FCSTD DOCUMENT  (FreeCAD 0.20R26155 (Git))
Label: AVX-009159010061911 
License: All rights reserved
LicenseURL: http://en.wikipedia.org/wiki/All_rights_reserved
objects: Sketcher::SketchObject×2, PartDesign::Body×1
note: 3 computed .brp shape members not serialized (recipe doc carries the construction recipe); baked Part::Feature solids carry a one-line shape summary decoded from their .brp

FEATURE [Sketcher::SketchObject] Sketch  label="Edge_Cuts_0.1"
  FullyConstrained = false
  MapMode = 5
  Support = -> [XY_Plane]
  sketch-geometry (7):
    g0: LineSegment StartX=0 StartY=5.09886 StartZ=0 EndX=3.7 EndY=5.09886 EndZ=0
    g1: ArcOfCircle CenterX=4 CenterY=2.29886 CenterZ=0 NormalX=0 NormalY=0 NormalZ=1 AngleXU=0 Radius=0.3 StartAngle=3.14159 EndAngle=6.28319
    g2: LineSegment StartX=3.7 StartY=5.09886 StartZ=0 EndX=3.7 EndY=2.29886 EndZ=0
    g3: LineSegment StartX=4.3 StartY=2.29886 StartZ=0 EndX=4.3 EndY=5.09886 EndZ=0
    g4: LineSegment StartX=4 StartY=5.09886 StartZ=0 EndX=4 EndY=2.29886 EndZ=0
    g5: LineSegment StartX=4.3 StartY=5.09886 StartZ=0 EndX=10 EndY=5.09886 EndZ=0
    g6: LineSegment StartX=3.7 StartY=5.09886 StartZ=0 EndX=4.3 EndY=5.09886 EndZ=0
  constraints (19):
    c: PointOnObject(g0,g-2)
    c: Horizontal(g0)
    c: DistanceX(g0,g5) = 10
    c: Tangent(g2,g1) = -1.5708
    c: Tangent(g1,g3) = -1.5708
    c: Coincident(g4,g1)
    c: Vertical(g4)
    c: Diameter(g1) = 0.6
    c: Coincident(g5,g3)
    c: Coincident(g0,g2)
    c: Vertical(g3)
    c: Vertical(g2)
    c: Horizontal(g5)
    c: Coincident(g6,g0)
    c: Coincident(g6,g3)
    c: Horizontal(g6)
    c: PointOnObject(g4,g6)
    c: DistanceY(g4,g4) = 2.8
    c: DistanceX(g0,g4) = 4
FEATURE [Sketcher::SketchObject] Sketch001  label="Pads_TH_SMD"
  ExternalGeometry = -> [Sketch]
  FullyConstrained = false
  MapMode = 5
  Support = -> [XY_Plane]
  sketch-geometry (26):
    g0: LineSegment StartX=0 StartY=4.59886 StartZ=0 EndX=10.0102 EndY=4.59886 EndZ=0
    g1: LineSegment StartX=0.5 StartY=4.59886 StartZ=0 EndX=1.5 EndY=4.59886 EndZ=0
    g2: LineSegment StartX=1.5 StartY=4.59886 StartZ=0 EndX=1.5 EndY=0.598863 EndZ=0
    g3: LineSegment StartX=1.5 StartY=0.598863 StartZ=0 EndX=0.5 EndY=0.598863 EndZ=0
    g4: LineSegment StartX=0.5 StartY=0.598863 StartZ=0 EndX=0.5 EndY=4.59886 EndZ=0
    g5: LineSegment StartX=2.5 StartY=4.59886 StartZ=0 EndX=3.5 EndY=4.59886 EndZ=0
    g6: LineSegment StartX=3.5 StartY=4.59886 StartZ=0 EndX=3.5 EndY=0.598863 EndZ=0
    g7: LineSegment StartX=3.5 StartY=0.598863 StartZ=0 EndX=2.5 EndY=0.598863 EndZ=0
    g8: LineSegment StartX=2.5 StartY=0.598863 StartZ=0 EndX=2.5 EndY=4.59886 EndZ=0
    g9: LineSegment StartX=4.5 StartY=4.59886 StartZ=0 EndX=5.5 EndY=4.59886 EndZ=0
    g10: LineSegment StartX=5.5 StartY=4.59886 StartZ=0 EndX=5.5 EndY=0.598863 EndZ=0
    g11: LineSegment StartX=5.5 StartY=0.598863 StartZ=0 EndX=4.5 EndY=0.598863 EndZ=0
    g12: LineSegment StartX=4.5 StartY=0.598863 StartZ=0 EndX=4.5 EndY=4.59886 EndZ=0
    g13: LineSegment StartX=6.5 StartY=4.59886 StartZ=0 EndX=7.5 EndY=4.59886 EndZ=0
    g14: LineSegment StartX=7.5 StartY=4.59886 StartZ=0 EndX=7.5 EndY=0.598863 EndZ=0
    g15: LineSegment StartX=7.5 StartY=0.598863 StartZ=0 EndX=6.5 EndY=0.598863 EndZ=0
    g16: LineSegment StartX=6.5 StartY=0.598863 StartZ=0 EndX=6.5 EndY=4.59886 EndZ=0
    g17: LineSegment StartX=8.5 StartY=4.59886 StartZ=0 EndX=9.5 EndY=4.59886 EndZ=0
    g18: LineSegment StartX=9.5 StartY=4.59886 StartZ=0 EndX=9.5 EndY=0.598863 EndZ=0
    g19: LineSegment StartX=9.5 StartY=0.598863 StartZ=0 EndX=8.5 EndY=0.598863 EndZ=0
    g20: LineSegment StartX=8.5 StartY=0.598863 StartZ=0 EndX=8.5 EndY=4.59886 EndZ=0
    g21: GeomPoint X=1 Y=0.598863 Z=0
    g22: GeomPoint X=3 Y=0.598863 Z=0
    g23: GeomPoint X=5 Y=0.598863 Z=0
    g24: GeomPoint X=7 Y=0.598863 Z=0
    g25: GeomPoint X=9 Y=0.598863 Z=0
  constraints (68):
    c: PointOnObject(g0,g-2)
    c: Horizontal(g0)
    c: Coincident(g1,g2)
    c: Coincident(g2,g3)
    c: Coincident(g3,g4)
    c: Coincident(g4,g1)
    c: Horizontal(g1)
    c: Horizontal(g3)
    c: Vertical(g2)
    c: Vertical(g4)
    c: PointOnObject(g1,g0)
    c: Coincident(g5,g6)
    c: Coincident(g6,g7)
    c: Coincident(g7,g8)
    c: Coincident(g8,g5)
    c: Horizontal(g5)
    c: Horizontal(g7)
    c: Vertical(g6)
    c: Vertical(g8)
    c: PointOnObject(g5,g0)
    c: Coincident(g9,g10)
    c: Coincident(g10,g11)
    c: Coincident(g11,g12)
    c: Coincident(g12,g9)
    c: Horizontal(g9)
    c: Horizontal(g11)
    c: Vertical(g10)
    c: Vertical(g12)
    c: PointOnObject(g9,g0)
    c: Coincident(g13,g14)
    c: Coincident(g14,g15)
    c: Coincident(g15,g16)
    c: Coincident(g16,g13)
    c: Horizontal(g13)
    c: Horizontal(g15)
    c: Vertical(g14)
    c: Vertical(g16)
    c: PointOnObject(g13,g0)
    c: Coincident(g17,g18)
    c: Coincident(g18,g19)
    c: Coincident(g19,g20)
    c: Coincident(g20,g17)
    c: Horizontal(g17)
    c: Horizontal(g19)
    c: Vertical(g18)
    c: Vertical(g20)
    c: PointOnObject(g17,g0)
    c: Equal(g3,g7)
    c: Equal(g7,g11)
    c: Equal(g11,g15)
    c: Equal(g15,g19)
    c: DistanceX(g19,g19) = 1
    c: Equal(g4,g8)
    c: Equal(g8,g12)
    c: Equal(g12,g16)
    c: Equal(g16,g20)
    c: DistanceY(g18,g18) = 4
    c: DistanceY(g0,g-3) = 0.5
    c: DistanceX(g21,g22) = 2
    c: Symmetric(g3,g3,g21)
    c: Symmetric(g7,g7,g22)
    c: Symmetric(g11,g11,g23)
    c: DistanceX(g22,g23) = 2
    c: Symmetric(g15,g15,g24)
    c: Symmetric(g19,g19,g25)
    c: DistanceX(g24,g25) = 2
    c: DistanceX(g23,g24) = 2
    c: DistanceX(g22,g-4) = 1
FEATURE [PartDesign::Body] Body
  Group = -> [Sketch,Sketch001]
  Origin = -> Origin
